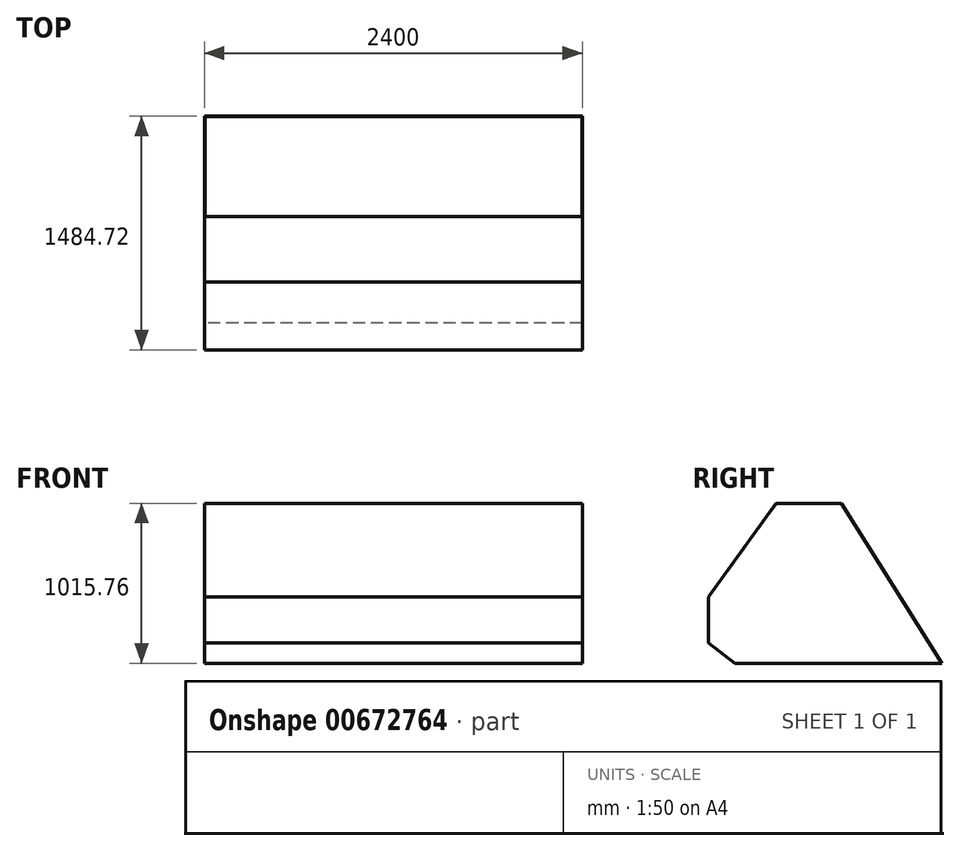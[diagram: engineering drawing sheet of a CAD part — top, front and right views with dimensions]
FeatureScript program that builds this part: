
annotation { "Feature Type Name" : "Feature", "Feature Type Description" : "" }
export const myFeature = defineFeature(function(context is Context, id is Id, definition is map)
    precondition{}
    {
        {
            var Q0;
            Q0=qCreatedBy(makeId("Right.planeOp"),FACE);
            var sketch = newSketch(context, id + "F0", { "sketchPlane" : qUnion([Q0])});
            skLineSegment(sketch, "E0", {"start": v(415.72, 352.24) * mm, "end": v(0, 352.24) * mm});
            skLineSegment(sketch, "E1", {"start": v(0, 352.24) * mm, "end": v(-430.06, -241.65) * mm});
            skLineSegment(sketch, "E2", {"start": v(-430.06, -241.65) * mm, "end": v(-430.06, -534.5) * mm});
            skLineSegment(sketch, "E3", {"start": v(-430.06, -534.5) * mm, "end": v(-260.08, -663.52) * mm});
            skLineSegment(sketch, "E4", {"start": v(-260.08, -663.52) * mm, "end": v(1054.66, -663.52) * mm});
            skLineSegment(sketch, "E5", {"start": v(1054.66, -663.52) * mm, "end": v(415.72, 352.24) * mm});
            skSolve(sketch);
        }
        {
            var Q0;
            Q0 = qSketchRegion(id + "F0", true);
            extrude(context, id + "F1", {"entities" : qUnion([Q0]), "depth" : 2400 * mm, "offsetDistance" : 25 * mm});
        }
        {
            var Q0;
            Q0=makeQuery(id+"F1.opExtrude","SWEPT_FACE",FACE,{"disambiguationData":[OSD([sQuery(id+"F0.wireOp",EDGE,"E5")])]});
            shell(context, id + "F2", {"entities" : qUnion([Q0]), "thickness" : 2.5 * mm});
        }
    });
